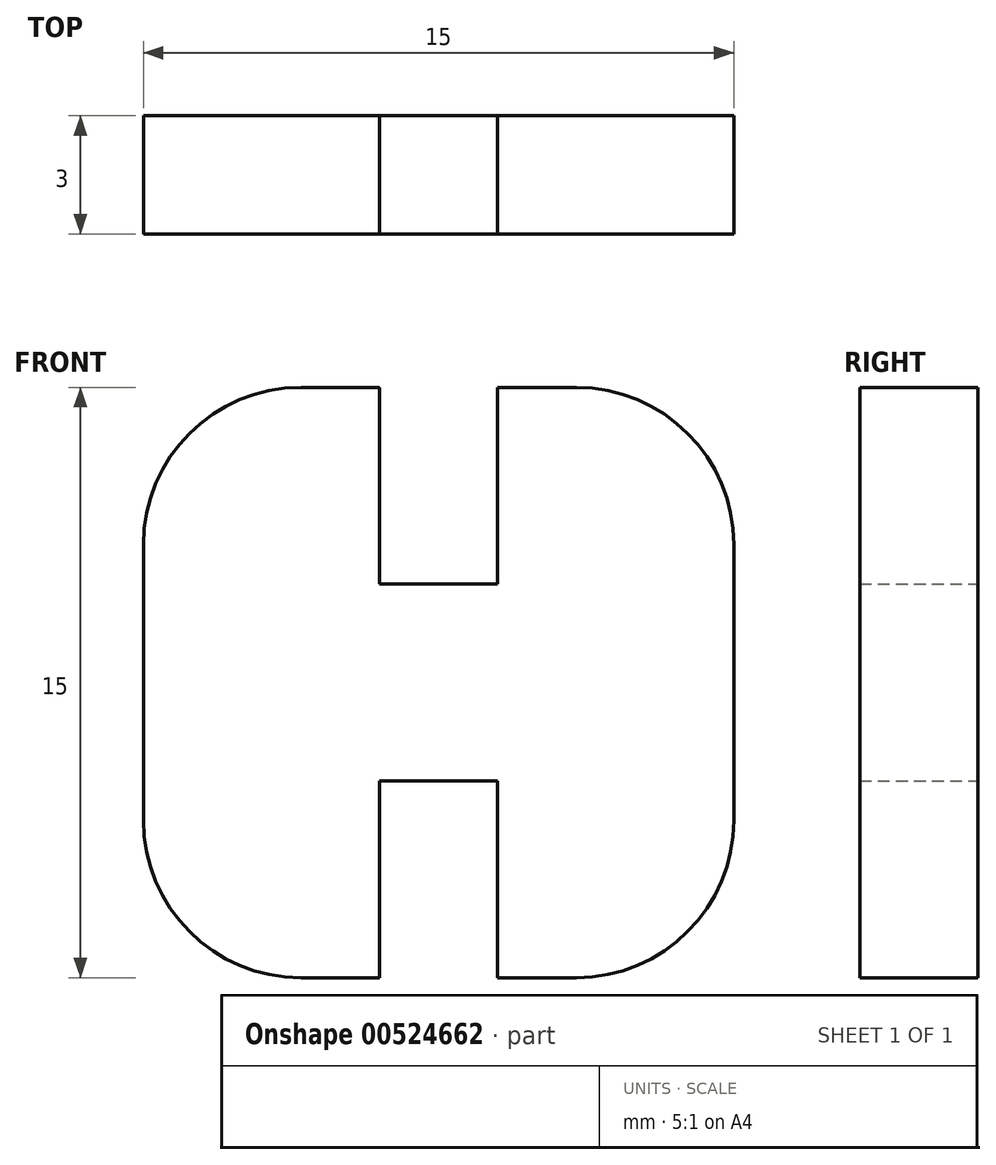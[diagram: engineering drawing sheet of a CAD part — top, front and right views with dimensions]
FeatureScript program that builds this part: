
annotation { "Feature Type Name" : "Feature", "Feature Type Description" : "" }
export const myFeature = defineFeature(function(context is Context, id is Id, definition is map)
    precondition{}
    {
        {
            var Q0;
            Q0=qCreatedBy(makeId("Front.planeOp"),FACE);
            var sketch = newSketch(context, id + "F0", { "sketchPlane" : qUnion([Q0])});
            skLineSegment(sketch, "E0", {"start": v(-6.76, 10.7) * mm, "end": v(-0.76, 10.7) * mm});
            skLineSegment(sketch, "E1", {"start": v(8.24, 10.7) * mm, "end": v(8.24, 25.7) * mm});
            skLineSegment(sketch, "E2", {"start": v(8.24, 25.7) * mm, "end": v(2.24, 25.7) * mm});
            skLineSegment(sketch, "E3", {"start": v(-6.76, 25.7) * mm, "end": v(-6.76, 10.7) * mm});
            skLineSegment(sketch, "E4", {"start": v(-0.76, 10.7) * mm, "end": v(-0.76, 15.7) * mm});
            skLineSegment(sketch, "E5", {"start": v(-0.76, 15.7) * mm, "end": v(2.24, 15.7) * mm});
            skLineSegment(sketch, "E6", {"start": v(2.24, 15.7) * mm, "end": v(2.24, 10.7) * mm});
            skLineSegment(sketch, "E7", {"start": v(2.24, 25.7) * mm, "end": v(2.24, 20.7) * mm});
            skLineSegment(sketch, "E8", {"start": v(2.24, 20.7) * mm, "end": v(-0.76, 20.7) * mm});
            skLineSegment(sketch, "E9", {"start": v(-0.76, 20.7) * mm, "end": v(-0.76, 25.7) * mm});
            skLineSegment(sketch, "E10.trimOffspring", {"start": v(-0.76, 25.7) * mm, "end": v(-6.76, 25.7) * mm});
            skLineSegment(sketch, "E11.trimOffspring", {"start": v(2.24, 10.7) * mm, "end": v(8.24, 10.7) * mm});
            skSolve(sketch);
        }
        {
            var Q0;
            Q0=makeQuery(id+"F0.imprint","IMPRINT",FACE,{"disambiguationData":[TD([[makeQuery(id+"F0.imprint","IMPRINT",EDGE,{"derivedFrom":sQuery(id+"F0.wireOp",EDGE,"E0")}),1.0]])]});
            extrude(context, id + "F1", {"entities" : qUnion([Q0]), "depth" : 3 * mm, "offsetDistance" : 25 * mm});
        }
        {
            var Q0;
            Q0=makeQuery(id+"F1.opExtrude","SWEPT_EDGE",EDGE,{"disambiguationData":[OSD([sQuery(id+"F0.wireOp",EDGE,"E1"),sQuery(id+"F0.wireOp",EDGE,"E2")])]});
            var Q1;
            Q1=makeQuery(id+"F1.opExtrude","SWEPT_EDGE",EDGE,{"disambiguationData":[OSD([sQuery(id+"F0.wireOp",EDGE,"E0"),sQuery(id+"F0.wireOp",EDGE,"E3")])]});
            var Q2;
            Q2=makeQuery(id+"F1.opExtrude","SWEPT_EDGE",EDGE,{"disambiguationData":[OSD([sQuery(id+"F0.wireOp",EDGE,"E3"),sQuery(id+"F0.wireOp",EDGE,"E10.trimOffspring")])]});
            var Q3;
            Q3=makeQuery(id+"F1.opExtrude","SWEPT_EDGE",EDGE,{"disambiguationData":[OSD([sQuery(id+"F0.wireOp",EDGE,"E1"),sQuery(id+"F0.wireOp",EDGE,"E11.trimOffspring")])]});
            fillet(context, id + "F2", {"entities" : qUnion([Q0, Q1, Q2, Q3]), "radius" : 4 * mm, "tangentPropagation" : true, "allowEdgeOverflow" : false});
        }
    });
